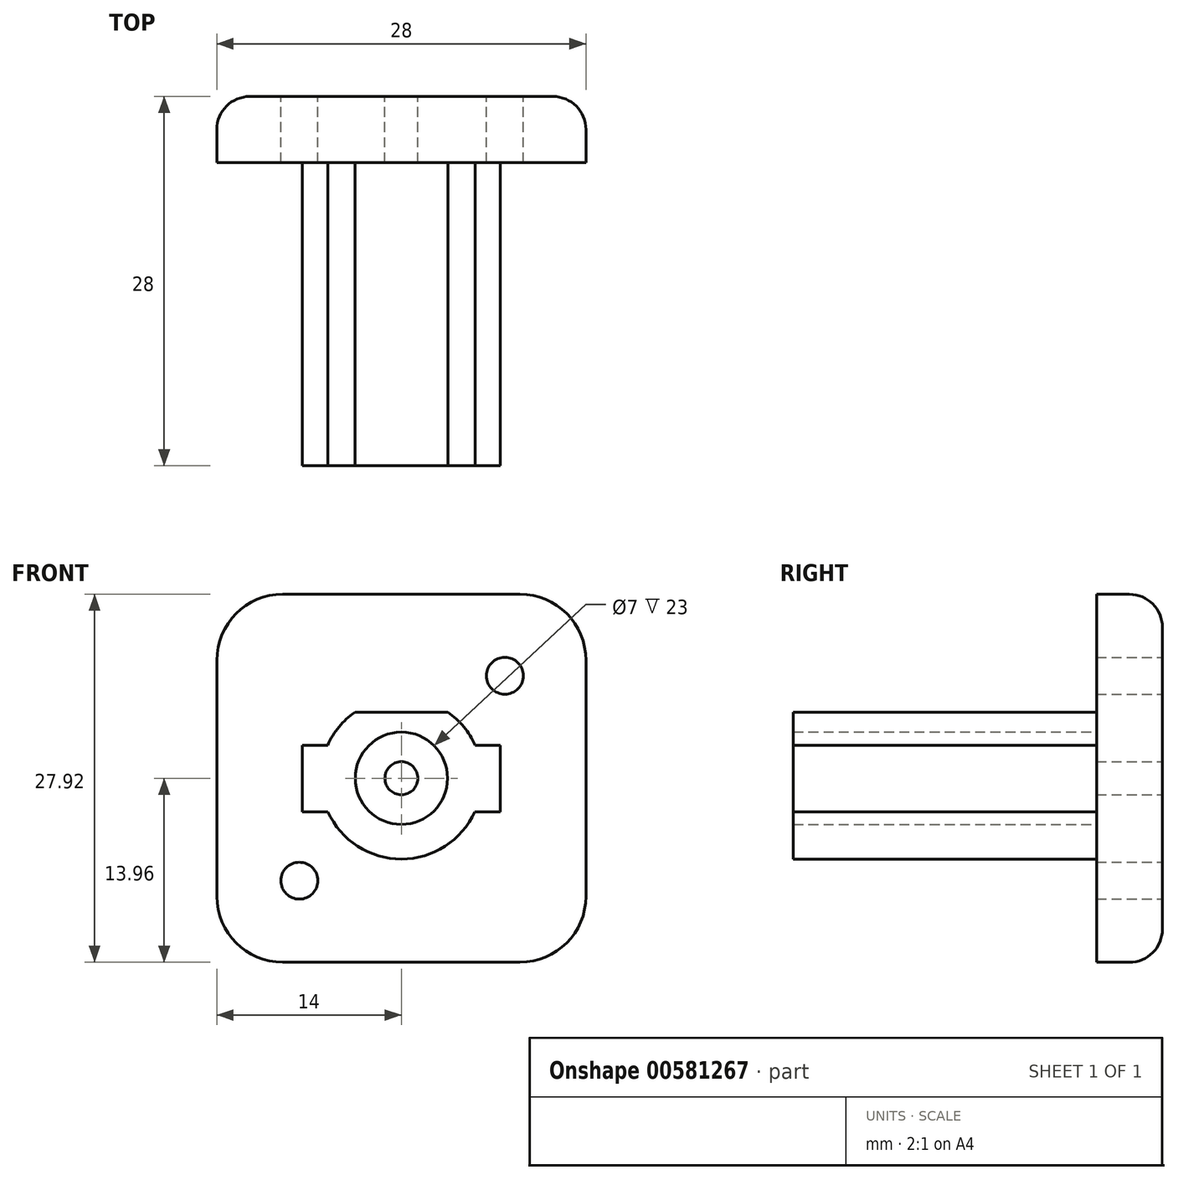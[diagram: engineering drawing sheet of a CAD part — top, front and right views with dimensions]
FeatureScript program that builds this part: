
annotation { "Feature Type Name" : "Feature", "Feature Type Description" : "" }
export const myFeature = defineFeature(function(context is Context, id is Id, definition is map)
    precondition{}
    {
        {
            var Q0;
            Q0=qCreatedBy(makeId("Front.planeOp"),FACE);
            var sketch = newSketch(context, id + "F0", { "sketchPlane" : qUnion([Q0])});
            skCircle(sketch, "E0", {"center": v(0, 0) * mm, "radius": 1.25 * mm});
            skCircle(sketch, "E1", {"center": v(0, 0) * mm, "radius": 3.5 * mm});
            skArc(sketch, "E2", {"start": v(-3.53, 5.01) * mm, "mid": v(-4.73, 3.9) * mm, "end": v(-5.6, 2.5) * mm});
            skLineSegment(sketch, "E3", {"start": v(-3.53, 5.01) * mm, "end": v(3.53, 5.01) * mm});
            skLineSegment(sketch, "E4.bottom", {"start": v(-7.5, 2.5) * mm, "end": v(-5.6, 2.5) * mm});
            skLineSegment(sketch, "E4.top", {"start": v(-7.5, -2.54) * mm, "end": v(-5.58, -2.54) * mm});
            skLineSegment(sketch, "E4.left", {"start": v(-7.5, 2.5) * mm, "end": v(-7.5, -2.54) * mm});
            skLineSegment(sketch, "E5.bottom", {"start": v(7.49, 2.5) * mm, "end": v(5.6, 2.5) * mm});
            skLineSegment(sketch, "E5.top", {"start": v(7.49, -2.54) * mm, "end": v(5.58, -2.54) * mm});
            skLineSegment(sketch, "E5.left", {"start": v(7.49, 2.5) * mm, "end": v(7.49, -2.54) * mm});
            skArc(sketch, "E6.trimOffspring", {"start": v(-5.58, -2.54) * mm, "mid": v(0, -6.13) * mm, "end": v(5.58, -2.54) * mm});
            skArc(sketch, "E7.trimOffspring", {"start": v(5.6, 2.5) * mm, "mid": v(4.73, 3.9) * mm, "end": v(3.53, 5.01) * mm});
            skPoint(sketch, "E8.orphan", {"position": v(5.1, -2.54) * mm});
            skPoint(sketch, "E4.right.end.orphan", {"position": v(-5.03, -2.54) * mm});
            skSolve(sketch);
        }
        {
            var Q0;
            Q0 = qSketchRegion(id + "F0", true);
            extrude(context, id + "F1", {"entities" : qUnion([Q0]), "depth" : 28 * mm, "offsetDistance" : 25 * mm});
        }
        {
            var Q0;
            Q0=qCreatedBy(makeId("Front.planeOp"),FACE);
            var sketch = newSketch(context, id + "F2", { "sketchPlane" : qUnion([Q0])});
            skCircle(sketch, "E9", {"center": v(7.85, 7.77) * mm, "radius": 1.4 * mm});
            skCircle(sketch, "E10", {"center": v(-7.74, -7.77) * mm, "radius": 1.4 * mm});
            skLineSegment(sketch, "E11.bottom", {"start": v(14, 13.96) * mm, "end": v(-14, 13.96) * mm});
            skLineSegment(sketch, "E11.top", {"start": v(14, -13.96) * mm, "end": v(-14, -13.96) * mm});
            skLineSegment(sketch, "E11.left", {"start": v(14, 13.96) * mm, "end": v(14, -13.96) * mm});
            skLineSegment(sketch, "E11.right", {"start": v(-14, 13.96) * mm, "end": v(-14, -13.96) * mm});
            skPoint(sketch, "E11.middle", {"position": v(0, 0) * mm});
            skSolve(sketch);
        }
        {
            var Q0;
            Q0 = qSketchRegion(id + "F2", true);
            extrude(context, id + "F3", {"entities" : qUnion([Q0]), "operationType" : NewBodyOperationType.ADD, "depth" : 5 * mm, "offsetDistance" : 25 * mm});
        }
        {
            var Q0;
            Q0=makeQuery(id+"F3.opExtrude","CAP_EDGE",EDGE,{"disambiguationData":[OSD([sQuery(id+"F2.wireOp",EDGE,"E11.left")])],"isStart":true});
            var Q1;
            Q1=makeQuery(id+"F3.opExtrude","CAP_EDGE",EDGE,{"disambiguationData":[OSD([sQuery(id+"F2.wireOp",EDGE,"E11.top")])],"isStart":true});
            var Q2;
            Q2=makeQuery(id+"F3.opExtrude","CAP_EDGE",EDGE,{"disambiguationData":[OSD([sQuery(id+"F2.wireOp",EDGE,"E11.right")])],"isStart":true});
            var Q3;
            Q3=makeQuery(id+"F3.opExtrude","CAP_EDGE",EDGE,{"disambiguationData":[OSD([sQuery(id+"F2.wireOp",EDGE,"E11.bottom")])],"isStart":true});
            fillet(context, id + "F4", {"entities" : qUnion([Q0, Q1, Q2, Q3]), "radius" : 2.5 * mm, "tangentPropagation" : true, "allowEdgeOverflow" : false});
        }
        {
            var Q0;
            Q0=makeQuery(id+"F3.opExtrude","SWEPT_EDGE",EDGE,{"disambiguationData":[OSD([sQuery(id+"F2.wireOp",EDGE,"E11.bottom"),sQuery(id+"F2.wireOp",EDGE,"E11.right")])]});
            var Q1;
            Q1=makeQuery(id+"F3.opExtrude","SWEPT_EDGE",EDGE,{"disambiguationData":[OSD([sQuery(id+"F2.wireOp",EDGE,"E11.bottom"),sQuery(id+"F2.wireOp",EDGE,"E11.left")])]});
            var Q2;
            Q2=makeQuery(id+"F3.opExtrude","SWEPT_EDGE",EDGE,{"disambiguationData":[OSD([sQuery(id+"F2.wireOp",EDGE,"E11.top"),sQuery(id+"F2.wireOp",EDGE,"E11.left")])]});
            var Q3;
            Q3=makeQuery(id+"F3.opExtrude","SWEPT_EDGE",EDGE,{"disambiguationData":[OSD([sQuery(id+"F2.wireOp",EDGE,"E11.top"),sQuery(id+"F2.wireOp",EDGE,"E11.right")])]});
            fillet(context, id + "F5", {"entities" : qUnion([Q0, Q1, Q2, Q3]), "radius" : 5 * mm, "tangentPropagation" : true, "allowEdgeOverflow" : false});
        }
        {
            var Q0;
            Q0=makeQuery(id+"F0.imprint","IMPRINT",FACE,{"disambiguationData":[TD([[makeQuery(id+"F0.imprint","IMPRINT",EDGE,{"derivedFrom":sQuery(id+"F0.wireOp",EDGE,"E0")}),1.0]])]});
            extrude(context, id + "F6", {"entities" : qUnion([Q0]), "operationType" : NewBodyOperationType.REMOVE, "depth" : 10 * mm, "offsetDistance" : 25 * mm});
        }
    });
